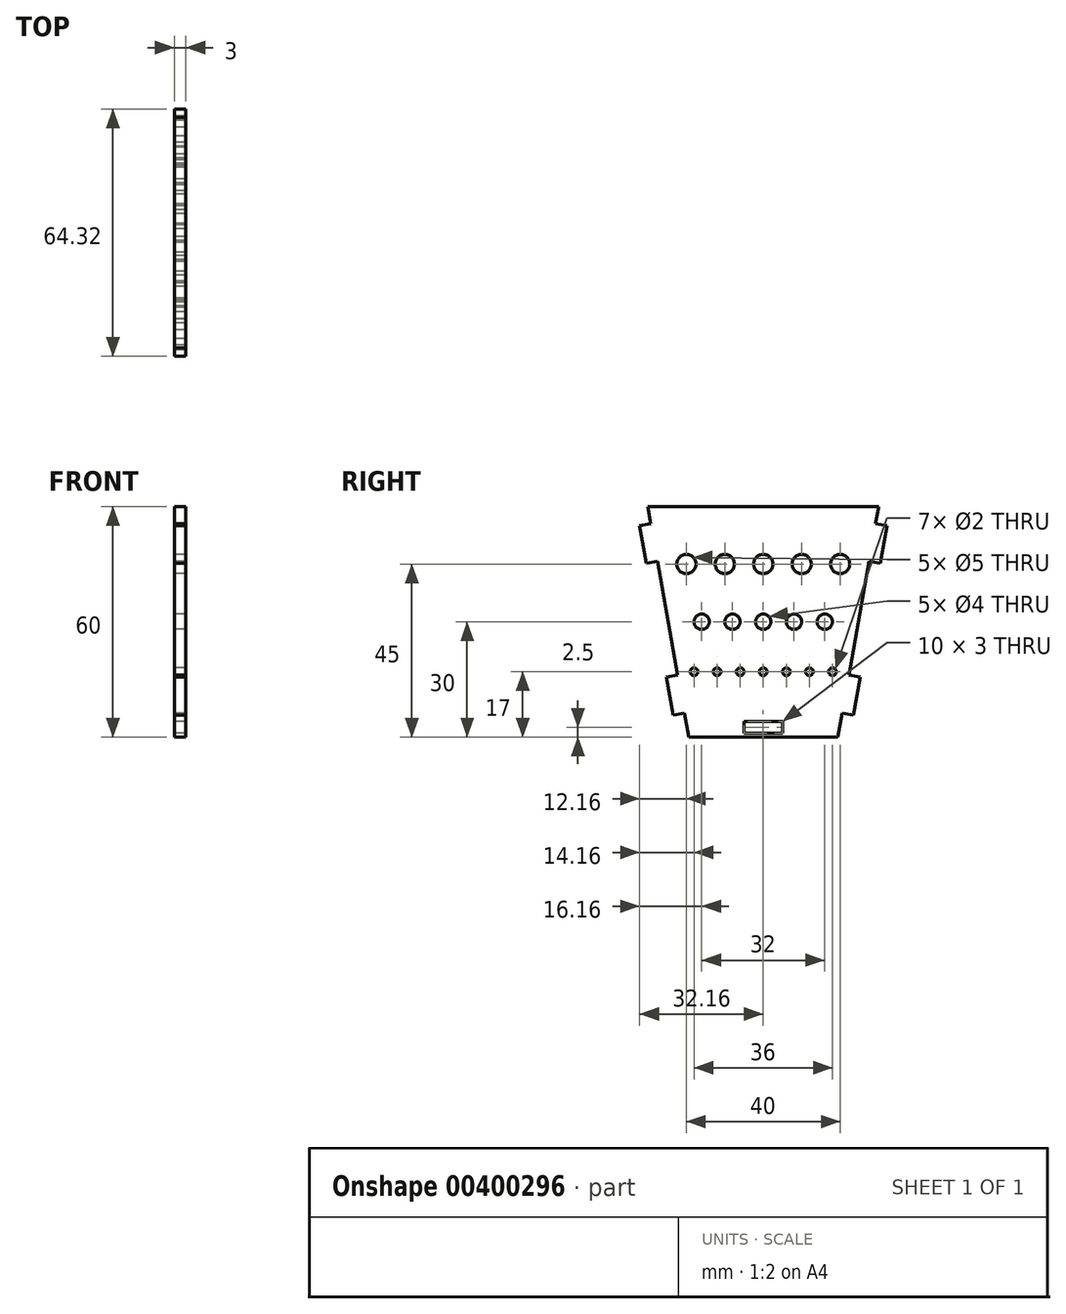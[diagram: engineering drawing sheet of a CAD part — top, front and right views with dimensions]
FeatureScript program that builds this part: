
annotation { "Feature Type Name" : "Feature", "Feature Type Description" : "" }
export const myFeature = defineFeature(function(context is Context, id is Id, definition is map)
    precondition{}
    {
        {
            var Q0;
            Q0=qCreatedBy(makeId("Right.planeOp"),FACE);
            var sketch = newSketch(context, id + "F0", { "sketchPlane" : qUnion([Q0])});
            skLineSegment(sketch, "E0", {"start": v(-19.42, 0) * mm, "end": v(19.42, 0) * mm});
            skLineSegment(sketch, "E1", {"start": v(19.42, 0) * mm, "end": v(20.53, 6.28) * mm});
            skLineSegment(sketch, "E2", {"start": v(20.53, 6.28) * mm, "end": v(23.48, 5.76) * mm});
            skLineSegment(sketch, "E3", {"start": v(23.48, 5.76) * mm, "end": v(25.22, 15.6) * mm});
            skLineSegment(sketch, "E4", {"start": v(25.22, 15.6) * mm, "end": v(22.26, 16.13) * mm});
            skLineSegment(sketch, "E5", {"start": v(22.26, 16.13) * mm, "end": v(27.47, 45.67) * mm});
            skLineSegment(sketch, "E6", {"start": v(27.47, 45.67) * mm, "end": v(30.43, 45.15) * mm});
            skLineSegment(sketch, "E7", {"start": v(30.43, 45.15) * mm, "end": v(32.16, 55) * mm});
            skLineSegment(sketch, "E8", {"start": v(32.16, 55) * mm, "end": v(29.21, 55.52) * mm});
            skLineSegment(sketch, "E9", {"start": v(29.21, 55.52) * mm, "end": v(30, 60) * mm});
            skLineSegment(sketch, "E10", {"start": v(30, 60) * mm, "end": v(-30, 60) * mm});
            skLineSegment(sketch, "E11", {"start": v(-30, 60) * mm, "end": v(-29.21, 55.52) * mm});
            skLineSegment(sketch, "E12", {"start": v(-29.21, 55.52) * mm, "end": v(-32.16, 55) * mm});
            skLineSegment(sketch, "E13", {"start": v(-32.16, 55) * mm, "end": v(-30.43, 45.15) * mm});
            skLineSegment(sketch, "E14", {"start": v(-30.43, 45.15) * mm, "end": v(-27.47, 45.67) * mm});
            skLineSegment(sketch, "E15", {"start": v(-27.47, 45.67) * mm, "end": v(-22.26, 16.13) * mm});
            skLineSegment(sketch, "E16", {"start": v(-22.26, 16.13) * mm, "end": v(-25.22, 15.6) * mm});
            skLineSegment(sketch, "E17", {"start": v(-25.22, 15.6) * mm, "end": v(-23.48, 5.76) * mm});
            skLineSegment(sketch, "E18", {"start": v(-23.48, 5.76) * mm, "end": v(-20.53, 6.28) * mm});
            skLineSegment(sketch, "E19", {"start": v(-20.53, 6.28) * mm, "end": v(-19.42, 0) * mm});
            skLineSegment(sketch, "E20", {"start": v(0, 0) * mm, "end": v(0, 55.34) * mm, "construction": true});
            skLineSegment(sketch, "E21.bottom", {"start": v(-5, 1) * mm, "end": v(5, 1) * mm});
            skLineSegment(sketch, "E21.top", {"start": v(-5, 4) * mm, "end": v(5, 4) * mm});
            skLineSegment(sketch, "E21.left", {"start": v(-5, 1) * mm, "end": v(-5, 4) * mm});
            skLineSegment(sketch, "E21.right", {"start": v(5, 1) * mm, "end": v(5, 4) * mm});
            skLineSegment(sketch, "E22", {"start": v(-24.94, 45) * mm, "end": v(25.4, 45) * mm, "construction": true});
            skLineSegment(sketch, "E23", {"start": v(-22.6, 30) * mm, "end": v(22.79, 30) * mm, "construction": true});
            skLineSegment(sketch, "E24", {"start": v(-20.77, 17) * mm, "end": v(20.44, 17) * mm, "construction": true});
            skCircle(sketch, "E25", {"center": v(-20, 45) * mm, "radius": 2.5 * mm});
            skCircle(sketch, "E26", {"center": v(-10, 45) * mm, "radius": 2.5 * mm});
            skCircle(sketch, "E27", {"center": v(-16, 30) * mm, "radius": 2 * mm});
            skCircle(sketch, "E28", {"center": v(-8, 30) * mm, "radius": 2 * mm});
            skCircle(sketch, "E29", {"center": v(-18, 17) * mm, "radius": 1 * mm});
            skCircle(sketch, "E30", {"center": v(-12, 17) * mm, "radius": 1 * mm});
            skCircle(sketch, "E31", {"center": v(-6, 17) * mm, "radius": 1 * mm});
            skCircle(sketch, "E32", {"center": v(0, 45) * mm, "radius": 2.5 * mm});
            skCircle(sketch, "E33", {"center": v(0, 30) * mm, "radius": 2 * mm});
            skCircle(sketch, "E34", {"center": v(0, 17) * mm, "radius": 1 * mm});
            skCircle(sketch, "E35.MirrorC", {"center": v(10, 45) * mm, "radius": 2.5 * mm});
            skCircle(sketch, "E36.MirrorC", {"center": v(20, 45) * mm, "radius": 2.5 * mm});
            skCircle(sketch, "E37.MirrorC", {"center": v(16, 30) * mm, "radius": 2 * mm});
            skCircle(sketch, "E38.MirrorC", {"center": v(8, 30) * mm, "radius": 2 * mm});
            skCircle(sketch, "E39.MirrorC", {"center": v(18, 17) * mm, "radius": 1 * mm});
            skCircle(sketch, "E40.MirrorC", {"center": v(12, 17) * mm, "radius": 1 * mm});
            skCircle(sketch, "E41.MirrorC", {"center": v(6, 17) * mm, "radius": 1 * mm});
            skSolve(sketch);
        }
        {
            var Q0;
            Q0=makeQuery(id+"F0.imprint","IMPRINT",FACE,{"disambiguationData":[TD([[makeQuery(id+"F0.imprint","IMPRINT",EDGE,{"derivedFrom":sQuery(id+"F0.wireOp",EDGE,"E0")}),1.0]])]});
            extrude(context, id + "F1", {"entities" : qUnion([Q0]), "depth" : 3 * mm});
        }
    });
